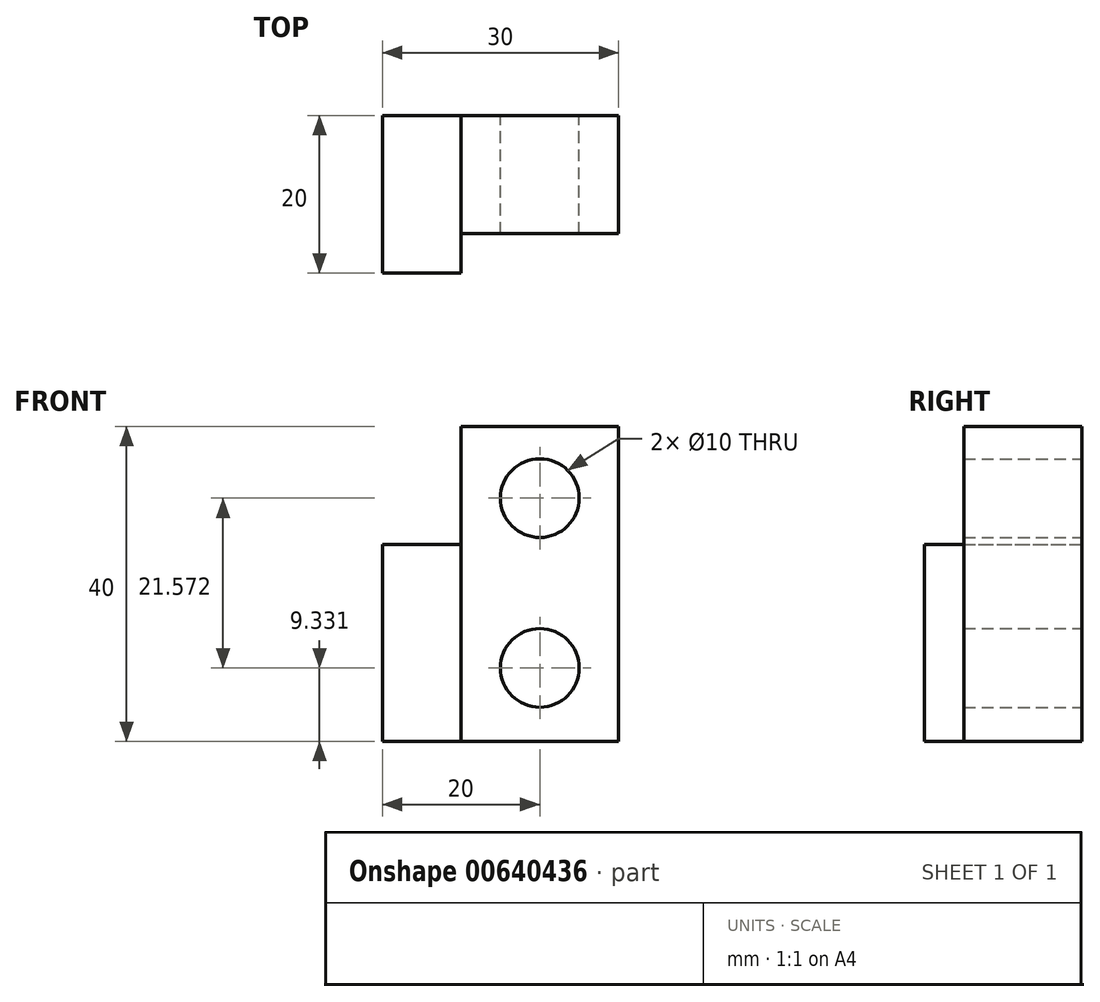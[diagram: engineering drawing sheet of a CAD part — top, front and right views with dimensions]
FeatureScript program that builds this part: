
annotation { "Feature Type Name" : "Feature", "Feature Type Description" : "" }
export const myFeature = defineFeature(function(context is Context, id is Id, definition is map)
    precondition{}
    {
        {
            var Q0;
            Q0=qCreatedBy(makeId("Front.planeOp"),FACE);
            var sketch = newSketch(context, id + "F0", { "sketchPlane" : qUnion([Q0])});
            skLineSegment(sketch, "E0.bottom", {"start": v(10, 20) * mm, "end": v(-10, 20) * mm});
            skLineSegment(sketch, "E0.top", {"start": v(10, -20) * mm, "end": v(-10, -20) * mm});
            skLineSegment(sketch, "E0.left", {"start": v(10, 20) * mm, "end": v(10, -20) * mm});
            skLineSegment(sketch, "E0.right", {"start": v(-10, 20) * mm, "end": v(-10, -20) * mm});
            skPoint(sketch, "E0.middle", {"position": v(0, 0) * mm});
            skSolve(sketch);
        }
        {
            var Q0;
            Q0 = qSketchRegion(id + "F0", true);
            extrude(context, id + "F1", {"entities" : qUnion([Q0]), "depth" : 15 * mm, "offsetDistance" : 25 * mm});
        }
        {
            var Q0;
            Q0=qCreatedBy(makeId("Front.planeOp"),FACE);
            var sketch = newSketch(context, id + "F2", { "sketchPlane" : qUnion([Q0])});
            skLineSegment(sketch, "E1.bottom", {"start": v(-10, -20) * mm, "end": v(-20, -20) * mm});
            skLineSegment(sketch, "E1.top", {"start": v(-10, 5) * mm, "end": v(-20, 5) * mm});
            skLineSegment(sketch, "E1.left", {"start": v(-10, -20) * mm, "end": v(-10, 5) * mm});
            skLineSegment(sketch, "E1.right", {"start": v(-20, -20) * mm, "end": v(-20, 5) * mm});
            skSolve(sketch);
        }
        {
            var Q0;
            Q0 = qSketchRegion(id + "F2", true);
            extrude(context, id + "F3", {"entities" : qUnion([Q0]), "operationType" : NewBodyOperationType.ADD, "depth" : 20 * mm, "offsetDistance" : 25 * mm});
        }
        {
            var Q0;
            Q0=qCreatedBy(makeId("Front.planeOp"),FACE);
            var sketch = newSketch(context, id + "F4", { "sketchPlane" : qUnion([Q0])});
            skCircle(sketch, "E2", {"center": v(0, 10.9) * mm, "radius": 5 * mm});
            skCircle(sketch, "E3", {"center": v(0, -10.67) * mm, "radius": 5 * mm});
            skSolve(sketch);
        }
        {
            var Q0;
            Q0 = qSketchRegion(id + "F4", true);
            extrude(context, id + "F5", {"entities" : qUnion([Q0]), "operationType" : NewBodyOperationType.REMOVE, "depth" : 15 * mm, "offsetDistance" : 25 * mm});
        }
    });
